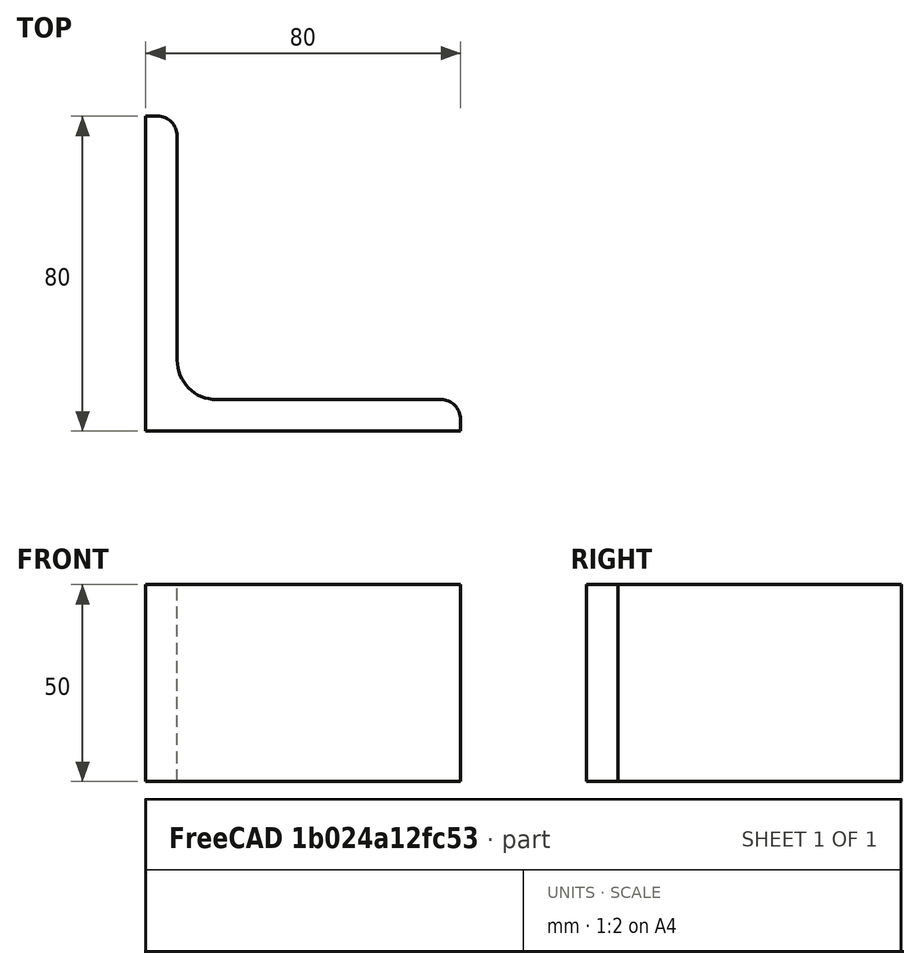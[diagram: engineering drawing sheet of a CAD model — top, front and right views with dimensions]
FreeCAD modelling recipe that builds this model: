
FCSTD DOCUMENT  (FreeCAD 0.15R4671 (Git))
Label: Angle Bar L80x80x8 EN10056 S235JR
License: All rights reserved
LicenseURL: http://en.wikipedia.org/wiki/All_rights_reserved
objects: Sketcher::SketchObject×1, Part::Extrusion×1
note: 2 computed .brp shape members not serialized (recipe doc carries the construction recipe); baked Part::Feature solids carry a one-line shape summary decoded from their .brp

FEATURE [Sketcher::SketchObject] Sketch
  sketch-geometry (9):
    g0: LineSegment StartX=0 StartY=0 StartZ=0 EndX=80 EndY=0 EndZ=0
    g1: LineSegment StartX=80 StartY=0 StartZ=0 EndX=80 EndY=3 EndZ=0
    g2: LineSegment StartX=75 StartY=8 StartZ=0 EndX=18 EndY=8 EndZ=0
    g3: LineSegment StartX=0 StartY=0 StartZ=0 EndX=0 EndY=80 EndZ=0
    g4: LineSegment StartX=0 StartY=80 StartZ=0 EndX=3 EndY=80 EndZ=0
    g5: LineSegment StartX=8 StartY=75 StartZ=0 EndX=8 EndY=18 EndZ=0
    g6: ArcOfCircle CenterX=18 CenterY=18 CenterZ=0 NormalX=0 NormalY=0 NormalZ=1 Radius=10 StartAngle=3.14159 EndAngle=4.71239
    g7: ArcOfCircle CenterX=3 CenterY=75 CenterZ=0 NormalX=0 NormalY=0 NormalZ=1 Radius=5 StartAngle=0 EndAngle=1.5708
    g8: ArcOfCircle CenterX=75 CenterY=3 CenterZ=0 NormalX=0 NormalY=0 NormalZ=1 Radius=5 StartAngle=0 EndAngle=1.5708
  constraints (23):
    c: Coincident(g0,g-1)
    c: Horizontal(g0)
    c: Coincident(g1,g0)
    c: Vertical(g1)
    c: Horizontal(g2)
    c: Coincident(g3,g-1)
    c: Vertical(g3)
    c: Coincident(g4,g3)
    c: Horizontal(g4)
    c: Vertical(g5)
    c: Tangent(g5,g6) = -1.5708
    c: Tangent(g2,g6) = 1.5708
    c: Tangent(g4,g7) = 1.5708
    c: Tangent(g5,g7) = 1.5708
    c: Tangent(g2,g8) = -1.5708
    c: Tangent(g1,g8) = -1.5708
    c: DistanceX(g0) = 80
    c: DistanceY(g3) = 80
    c: DistanceY(g0,g2) = 8
    c: DistanceX(g3,g5) = 8
    c: Radius(g6) = 10
    c: Radius(g8) = 5
    c: Radius(g7) = 5
FEATURE [Part::Extrusion] Extrude  label="Angle Bar L80x80x8 EN10056 S235JR"
  Base = -> Sketch
  Dir = (0,0,50)
  Solid = true
